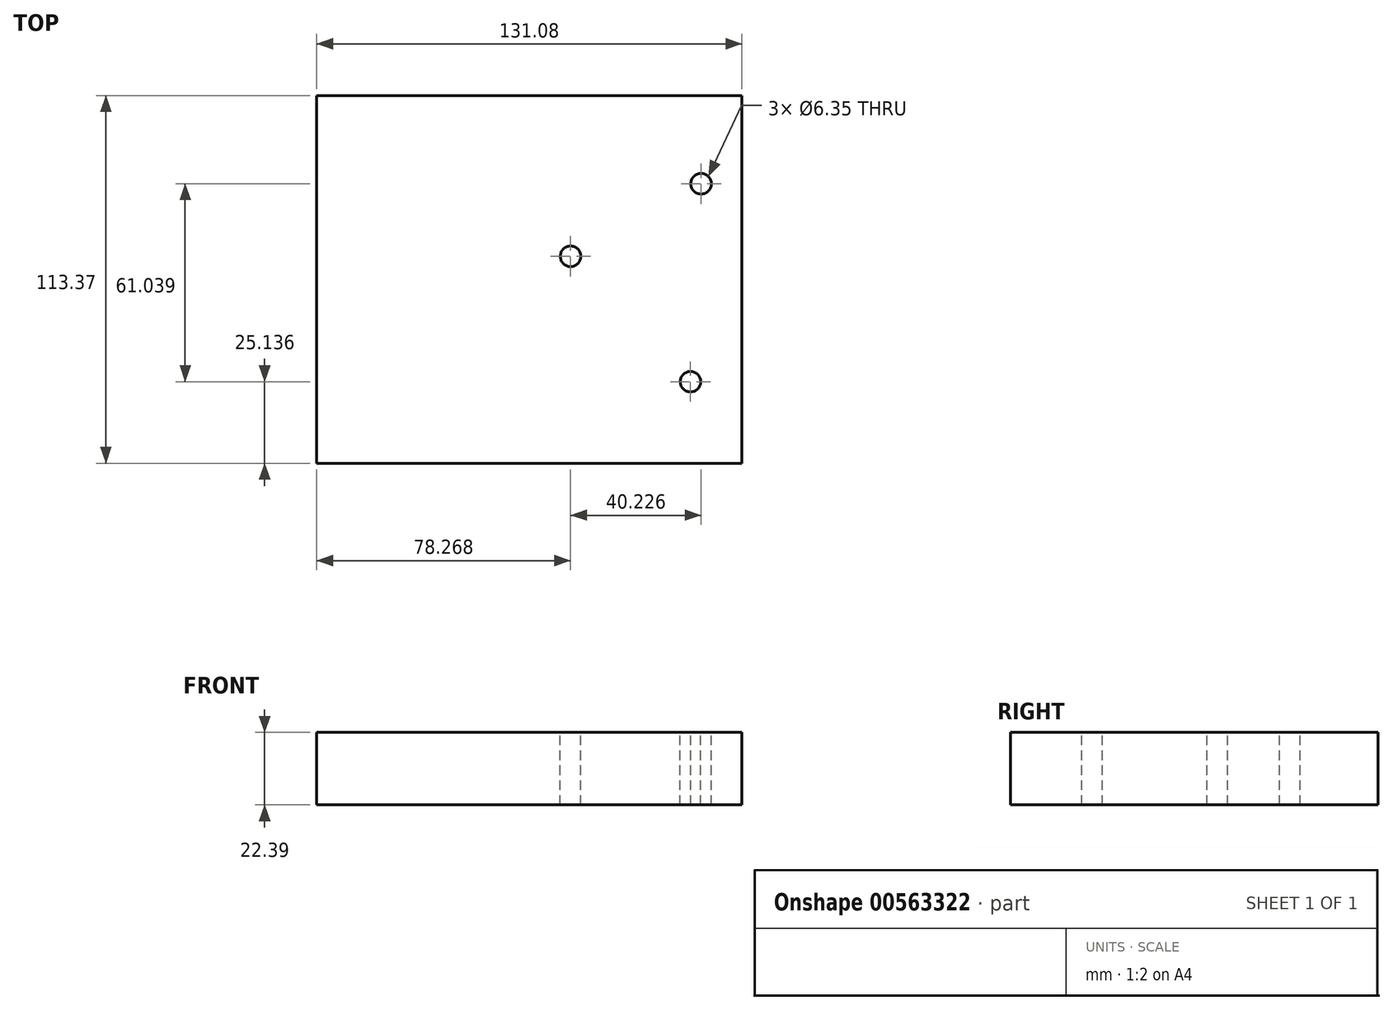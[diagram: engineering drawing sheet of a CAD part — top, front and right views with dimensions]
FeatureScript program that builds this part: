
annotation { "Feature Type Name" : "Feature", "Feature Type Description" : "" }
export const myFeature = defineFeature(function(context is Context, id is Id, definition is map)
    precondition{}
    {
        {
            var Q0;
            Q0=qCreatedBy(makeId("Front.planeOp"),FACE);
            var sketch = newSketch(context, id + "F0", { "sketchPlane" : qUnion([Q0])});
            skLineSegment(sketch, "E0.bottom", {"start": v(34.74, 33.35) * mm, "end": v(-96.34, 33.35) * mm});
            skLineSegment(sketch, "E0.top", {"start": v(34.74, 10.96) * mm, "end": v(-96.34, 10.96) * mm});
            skLineSegment(sketch, "E0.left", {"start": v(34.74, 33.35) * mm, "end": v(34.74, 10.96) * mm});
            skLineSegment(sketch, "E0.right", {"start": v(-96.34, 33.35) * mm, "end": v(-96.34, 10.96) * mm});
            skPoint(sketch, "E0.middle", {"position": v(-30.8, 22.16) * mm});
            skSolve(sketch);
        }
        {
            var Q0;
            Q0 = qSketchRegion(id + "F0", true);
            extrude(context, id + "F1", {"entities" : qUnion([Q0]), "depth" : 113.37 * mm, "offsetDistance" : 25.4 * mm});
        }
        {
            var Q0;
            Q0=makeQuery(id+"F1.opExtrude","SWEPT_FACE",FACE,{"disambiguationData":[OSD([sQuery(id+"F0.wireOp",EDGE,"E0.bottom")])]});
            var sketch = newSketch(context, id + "F2", { "sketchPlane" : qUnion([Q0])});
            skPoint(sketch, "E1", {"position": v(22.15, -27.2) * mm});
            skPoint(sketch, "E2", {"position": v(18.89, -88.23) * mm});
            skPoint(sketch, "E3", {"position": v(-18.07, -49.56) * mm});
            skSolve(sketch);
        }
        {
            var Q0;
            Q0=sQuery(id+"F2.wireOp",VERTEX,"E1");
            var Q1;
            Q1=sQuery(id+"F2.wireOp",VERTEX,"E3");
            var Q2;
            Q2=sQuery(id+"F2.wireOp",VERTEX,"E2");
            var Q3;
            Q3=makeQuery(id+"F1.opExtrude","SWEPT_BODY",BODY,{"disambiguationData":[OSD([sQuery(id+"F0.wireOp",EDGE,"E0.bottom"),sQuery(id+"F0.wireOp",EDGE,"E0.top"),sQuery(id+"F0.wireOp",EDGE,"E0.left"),sQuery(id+"F0.wireOp",EDGE,"E0.right")])]});
            hole(context, id + "F3", {"style" : HoleStyle.SIMPLE, "endStyle" : HoleEndStyle.THROUGH, "holeDiameter" : 6.35 * mm, "isTappedThrough" : true, "tappedDepth" : 12.7 * mm, "tapClearance" : 3, "locations" : qUnion([Q0, Q1, Q2]), "scope" : qUnion([Q3])});
        }
    });
